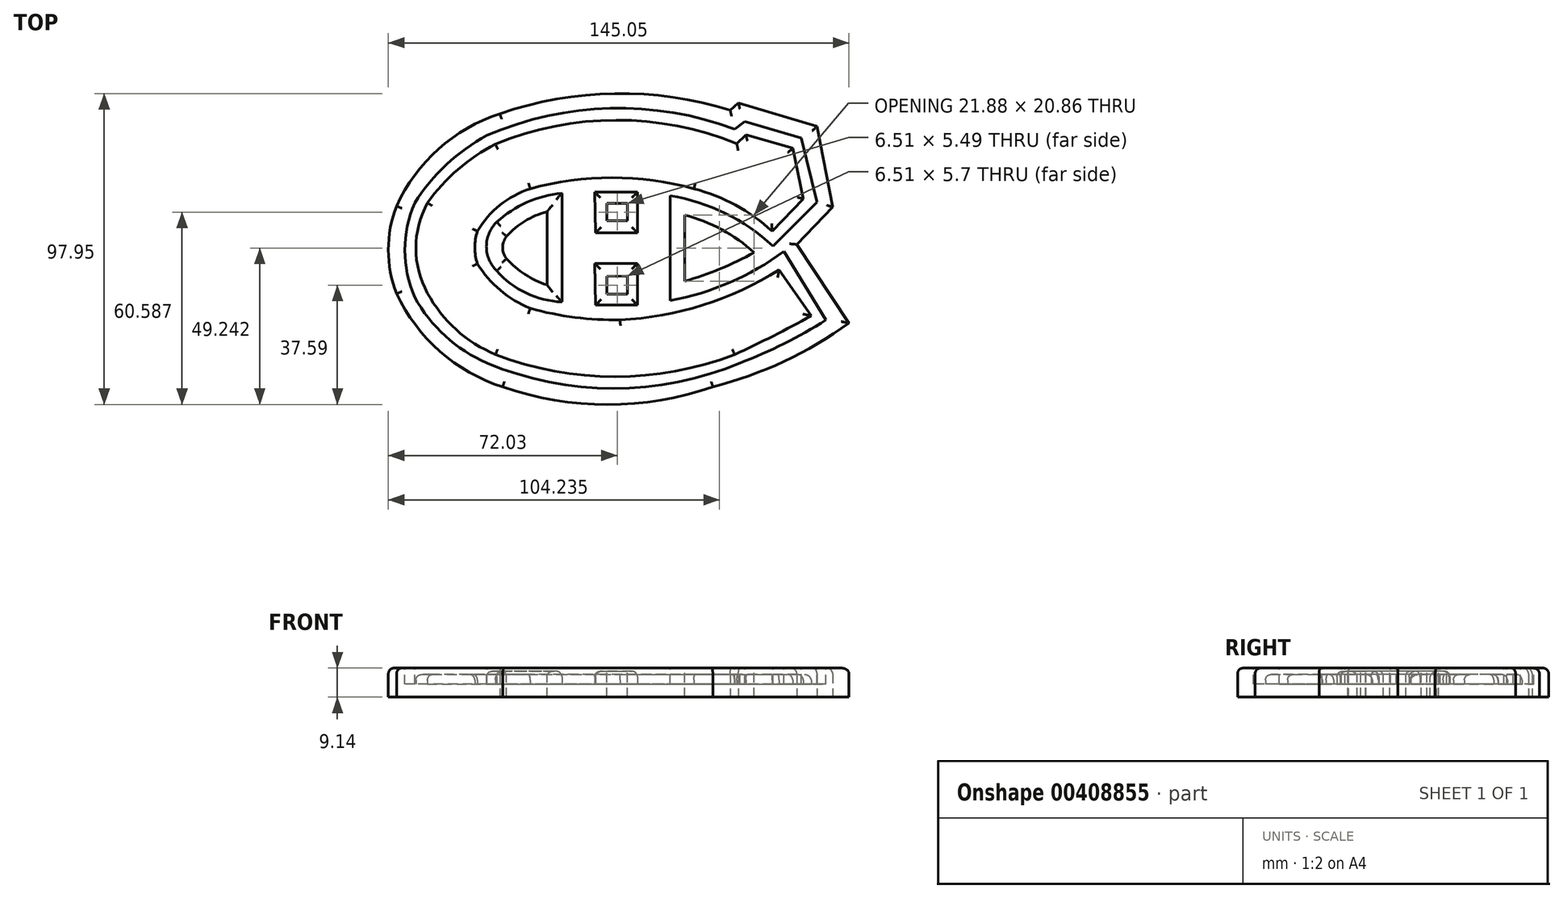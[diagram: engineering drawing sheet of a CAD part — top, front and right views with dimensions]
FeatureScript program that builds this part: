
annotation { "Feature Type Name" : "Feature", "Feature Type Description" : "" }
export const myFeature = defineFeature(function(context is Context, id is Id, definition is map)
    precondition{}
    {
        {
            var Q0;
            Q0=qCreatedBy(makeId("Top.planeOp"),FACE);
            var sketch = newSketch(context, id + "F0", { "sketchPlane" : qUnion([Q0])});
            skArc(sketch, "E0", {"start": v(34.63, 46.82) * mm, "mid": v(-1.72, 52.03) * mm, "end": v(-37.9, 45.67) * mm});
            skArc(sketch, "E1", {"start": v(-37.9, 45.67) * mm, "mid": v(-57.2, 34.55) * mm, "end": v(-70.42, 16.6) * mm});
            skArc(sketch, "E2", {"start": v(-70.42, 16.6) * mm, "mid": v(-73, 2.79) * mm, "end": v(-70.42, -11.03) * mm});
            skArc(sketch, "E3", {"start": v(-70.42, -11.03) * mm, "mid": v(-56.74, -29.14) * mm, "end": v(-37.03, -40.38) * mm});
            skArc(sketch, "E4", {"start": v(-37.03, -40.38) * mm, "mid": v(-3.93, -45.9) * mm, "end": v(29.16, -40.38) * mm});
            skArc(sketch, "E5", {"start": v(29.16, -40.38) * mm, "mid": v(51.55, -32.32) * mm, "end": v(72.05, -20.24) * mm});
            skLineSegment(sketch, "E6", {"start": v(55.64, 4.52) * mm, "end": v(72.05, -20.24) * mm});
            skLineSegment(sketch, "E7", {"start": v(55.64, 4.52) * mm, "end": v(66.87, 16.32) * mm});
            skLineSegment(sketch, "E8", {"start": v(66.87, 16.32) * mm, "end": v(61.97, 41.64) * mm});
            skLineSegment(sketch, "E9", {"start": v(61.97, 41.64) * mm, "end": v(37.22, 49.13) * mm});
            skLineSegment(sketch, "E10", {"start": v(37.22, 49.13) * mm, "end": v(34.63, 46.82) * mm});
            skSolve(sketch);
        }
        {
            var Q0;
            Q0=makeQuery(id+"F0.imprint","IMPRINT",FACE,{"disambiguationData":[TD([[makeQuery(id+"F0.imprint","IMPRINT",EDGE,{"derivedFrom":sQuery(id+"F0.wireOp",EDGE,"E0")}),1.0]])]});
            extrude(context, id + "F1", {"entities" : qUnion([Q0]), "depth" : 9.14 * mm});
        }
        {
            var Q0;
            Q0=makeQuery(id+"F1.opExtrude","CAP_FACE",FACE,{"disambiguationData":[OSD([sQuery(id+"F0.wireOp",EDGE,"E0"),sQuery(id+"F0.wireOp",EDGE,"E1"),sQuery(id+"F0.wireOp",EDGE,"E2"),sQuery(id+"F0.wireOp",EDGE,"E3"),sQuery(id+"F0.wireOp",EDGE,"E4"),sQuery(id+"F0.wireOp",EDGE,"E5"),sQuery(id+"F0.wireOp",EDGE,"E6"),sQuery(id+"F0.wireOp",EDGE,"E7"),sQuery(id+"F0.wireOp",EDGE,"E8"),sQuery(id+"F0.wireOp",EDGE,"E9"),sQuery(id+"F0.wireOp",EDGE,"E10")])],"isStart":false});
            var sketch = newSketch(context, id + "F2", { "sketchPlane" : qUnion([Q0])});
            skArc(sketch, "E11", {"start": v(36, 40.87) * mm, "mid": v(-3.18, 47.38) * mm, "end": v(-41.99, 38.85) * mm});
            skArc(sketch, "E12", {"start": v(-41.99, 38.85) * mm, "mid": v(-54.71, 29.65) * mm, "end": v(-64.72, 17.56) * mm});
            skArc(sketch, "E13", {"start": v(-64.72, 17.56) * mm, "mid": v(-67.78, 2.73) * mm, "end": v(-64.72, -12.09) * mm});
            skArc(sketch, "E14", {"start": v(-64.72, -12.09) * mm, "mid": v(-55.07, -24.33) * mm, "end": v(-41.99, -32.8) * mm});
            skArc(sketch, "E15", {"start": v(-41.99, -32.8) * mm, "mid": v(-2.12, -40.85) * mm, "end": v(37.74, -32.8) * mm});
            skArc(sketch, "E16", {"start": v(37.74, -32.8) * mm, "mid": v(51.6, -26.7) * mm, "end": v(64.8, -19.28) * mm});
            skLineSegment(sketch, "E17", {"start": v(48.1, 4.03) * mm, "end": v(61.91, 17.84) * mm});
            skLineSegment(sketch, "E18", {"start": v(61.91, 17.84) * mm, "end": v(57.02, 38) * mm});
            skLineSegment(sketch, "E19", {"start": v(57.02, 38) * mm, "end": v(39.18, 43.17) * mm});
            skLineSegment(sketch, "E20", {"start": v(39.18, 43.17) * mm, "end": v(36, 40.87) * mm});
            skLineSegment(sketch, "E21", {"start": v(64.8, -19.28) * mm, "end": v(51.55, 2.3) * mm});
            skArc(sketch, "E22", {"start": v(15.77, -13.17) * mm, "mid": v(34.54, -7.45) * mm, "end": v(51.55, 2.3) * mm});
            skLineSegment(sketch, "E23", {"start": v(15.77, -13.17) * mm, "end": v(15.77, 19.88) * mm});
            skArc(sketch, "E24", {"start": v(48.1, 4.03) * mm, "mid": v(33.1, 14.32) * mm, "end": v(15.77, 19.88) * mm});
            skSolve(sketch);
        }
        {
            var Q0;
            Q0 = qSketchRegion(id + "F2", true);
            extrude(context, id + "F3", {"entities" : qUnion([Q0]), "operationType" : NewBodyOperationType.REMOVE, "depth" : 7.62 * mm});
        }
        {
            var Q0;
            Q0 = qSketchRegion(id + "F2", true);
            extrude(context, id + "F4", {"entities" : qUnion([Q0]), "operationType" : NewBodyOperationType.REMOVE, "oppositeDirection" : true, "depth" : 5.08 * mm});
        }
        {
            var Q0;
            Q0=makeQuery(id+"F4.boolean.opBoolean","COPY",FACE,{"derivedFrom":makeQuery(id+"F4.opExtrude","CAP_FACE",FACE,{"disambiguationData":[OSD([sQuery(id+"F2.wireOp",EDGE,"E11"),sQuery(id+"F2.wireOp",EDGE,"E12"),sQuery(id+"F2.wireOp",EDGE,"E13"),sQuery(id+"F2.wireOp",EDGE,"E14"),sQuery(id+"F2.wireOp",EDGE,"E15"),sQuery(id+"F2.wireOp",EDGE,"E16"),sQuery(id+"F2.wireOp",EDGE,"E17"),sQuery(id+"F2.wireOp",EDGE,"E18"),sQuery(id+"F2.wireOp",EDGE,"E19"),sQuery(id+"F2.wireOp",EDGE,"E20"),sQuery(id+"F2.wireOp",EDGE,"E21"),sQuery(id+"F2.wireOp",EDGE,"E22"),sQuery(id+"F2.wireOp",EDGE,"E23"),sQuery(id+"F2.wireOp",EDGE,"E24")])],"isStart":false})});
            var sketch = newSketch(context, id + "F5", { "sketchPlane" : qUnion([Q0])});
            skLineSegment(sketch, "E25", {"start": v(-18.34, 20.64) * mm, "end": v(-18.34, -13.58) * mm});
            skLineSegment(sketch, "E26", {"start": v(-8.05, 20.99) * mm, "end": v(5.45, 20.99) * mm});
            skLineSegment(sketch, "E27", {"start": v(5.45, 20.99) * mm, "end": v(5.45, 8.15) * mm});
            skLineSegment(sketch, "E28", {"start": v(5.45, 8.15) * mm, "end": v(-7.73, 8.15) * mm});
            skLineSegment(sketch, "E29", {"start": v(-7.73, 8.15) * mm, "end": v(-8.05, 20.99) * mm});
            skLineSegment(sketch, "E30", {"start": v(-8.07, -1.43) * mm, "end": v(5.45, -1.43) * mm});
            skLineSegment(sketch, "E31", {"start": v(5.45, -1.43) * mm, "end": v(5.45, -14.6) * mm});
            skLineSegment(sketch, "E32", {"start": v(5.45, -14.6) * mm, "end": v(-7.73, -14.6) * mm});
            skLineSegment(sketch, "E33", {"start": v(-7.73, -14.6) * mm, "end": v(-8.07, -1.43) * mm});
            skArc(sketch, "E34", {"start": v(-18.34, 20.64) * mm, "mid": v(-29.35, 17.8) * mm, "end": v(-38.87, 11.57) * mm});
            skArc(sketch, "E35", {"start": v(-38.87, 11.57) * mm, "mid": v(-42.12, 3.87) * mm, "end": v(-38.87, -3.83) * mm});
            skArc(sketch, "E36", {"start": v(-38.87, -3.83) * mm, "mid": v(-29.6, -10.8) * mm, "end": v(-18.34, -13.58) * mm});
            skSolve(sketch);
        }
        {
            var Q0;
            Q0 = qSketchRegion(id + "F5", true);
            extrude(context, id + "F6", {"entities" : qUnion([Q0]), "operationType" : NewBodyOperationType.ADD, "depth" : 4.06 * mm});
        }
        {
            var Q0;
            {var subQ0=sQuery(id+"F2.wireOp",EDGE,"E24");var subQ1=sQuery(id+"F2.wireOp",EDGE,"E23");var subQ2=sQuery(id+"F2.wireOp",EDGE,"E22");var subQ3=sQuery(id+"F2.wireOp",EDGE,"E21");var subQ4=sQuery(id+"F2.wireOp",EDGE,"E14");var subQ5=sQuery(id+"F2.wireOp",EDGE,"E13");var subQ6=sQuery(id+"F2.wireOp",EDGE,"E12");var subQ7=sQuery(id+"F2.wireOp",EDGE,"E11");var subQ8=sQuery(id+"F2.wireOp",EDGE,"E15");var subQ9=sQuery(id+"F2.wireOp",EDGE,"E16");var subQ10=sQuery(id+"F2.wireOp",EDGE,"E17");var subQ11=sQuery(id+"F2.wireOp",EDGE,"E18");var subQ12=sQuery(id+"F2.wireOp",EDGE,"E19");var subQ13=sQuery(id+"F2.wireOp",EDGE,"E20");Q0=makeQuery(id+"F6.boolean.opBoolean","SPLIT",FACE,{"disambiguationData":[TD([makeQuery(id+"F4.boolean.opBoolean","COPY",FACE,{"derivedFrom":makeQuery(id+"F4.opExtrude","SWEPT_FACE",FACE,{"disambiguationData":[OSD([subQ7])]})})])],"derivedFrom":makeQuery(id+"F4.boolean.opBoolean","COPY",FACE,{"derivedFrom":makeQuery(id+"F4.opExtrude","CAP_FACE",FACE,{"disambiguationData":[OSD([subQ7,subQ6,subQ5,subQ4,subQ8,subQ9,subQ10,subQ11,subQ12,subQ13,subQ3,subQ2,subQ1,subQ0])],"isStart":false})})});}
            var sketch = newSketch(context, id + "F7", { "sketchPlane" : qUnion([Q0])});
            skArc(sketch, "E37", {"start": v(36.7, 36.24) * mm, "mid": v(-1.3, 43.67) * mm, "end": v(-39.27, 36.07) * mm});
            skArc(sketch, "E38", {"start": v(-39.27, 36.07) * mm, "mid": v(-51.09, 28.12) * mm, "end": v(-60.67, 17.59) * mm});
            skArc(sketch, "E39", {"start": v(-60.67, 17.59) * mm, "mid": v(-64.33, 3.38) * mm, "end": v(-60.67, -10.82) * mm});
            skArc(sketch, "E40", {"start": v(-60.67, -10.82) * mm, "mid": v(-51.63, -22.33) * mm, "end": v(-39.27, -30.16) * mm});
            skArc(sketch, "E41", {"start": v(-39.27, -30.16) * mm, "mid": v(-1.63, -37.13) * mm, "end": v(36, -30.16) * mm});
            skArc(sketch, "E42", {"start": v(36, -30.16) * mm, "mid": v(48.18, -24.29) * mm, "end": v(60.15, -18) * mm});
            skArc(sketch, "E43", {"start": v(0, -19.2) * mm, "mid": v(26.06, -14.62) * mm, "end": v(50.06, -3.46) * mm});
            skArc(sketch, "E44", {"start": v(-28.32, -15.61) * mm, "mid": v(-14.3, -18.45) * mm, "end": v(0, -19.2) * mm});
            skArc(sketch, "E45", {"start": v(-44.92, -1.58) * mm, "mid": v(-37.74, -9.92) * mm, "end": v(-28.32, -15.61) * mm});
            skArc(sketch, "E46", {"start": v(-44.92, 8.69) * mm, "mid": v(-45.77, 3.55) * mm, "end": v(-44.92, -1.58) * mm});
            skArc(sketch, "E47", {"start": v(-28.32, 22.04) * mm, "mid": v(-37.86, 16.9) * mm, "end": v(-44.92, 8.69) * mm});
            skArc(sketch, "E48", {"start": v(23.19, 22.04) * mm, "mid": v(-2.57, 25.54) * mm, "end": v(-28.32, 22.04) * mm});
            skArc(sketch, "E49", {"start": v(47.83, 8.69) * mm, "mid": v(36.34, 16.9) * mm, "end": v(23.19, 22.04) * mm});
            skLineSegment(sketch, "E50", {"start": v(36.7, 36.24) * mm, "end": v(39.55, 39.08) * mm});
            skLineSegment(sketch, "E51", {"start": v(39.55, 39.08) * mm, "end": v(54.3, 34.8) * mm});
            skLineSegment(sketch, "E52", {"start": v(54.3, 34.8) * mm, "end": v(57.66, 18.83) * mm});
            skLineSegment(sketch, "E53", {"start": v(57.66, 18.83) * mm, "end": v(47.83, 8.69) * mm});
            skLineSegment(sketch, "E54", {"start": v(50.06, -3.46) * mm, "end": v(60.15, -18) * mm});
            skSolve(sketch);
        }
        {
            var Q0;
            Q0 = qSketchRegion(id + "F7", true);
            extrude(context, id + "F8", {"entities" : qUnion([Q0]), "operationType" : NewBodyOperationType.ADD, "depth" : 3.05 * mm});
        }
        {
            var Q0;
            Q0=makeQuery(id+"F1.opExtrude","CAP_FACE",FACE,{"disambiguationData":[OSD([sQuery(id+"F0.wireOp",EDGE,"E0"),sQuery(id+"F0.wireOp",EDGE,"E1"),sQuery(id+"F0.wireOp",EDGE,"E2"),sQuery(id+"F0.wireOp",EDGE,"E3"),sQuery(id+"F0.wireOp",EDGE,"E4"),sQuery(id+"F0.wireOp",EDGE,"E5"),sQuery(id+"F0.wireOp",EDGE,"E6"),sQuery(id+"F0.wireOp",EDGE,"E7"),sQuery(id+"F0.wireOp",EDGE,"E8"),sQuery(id+"F0.wireOp",EDGE,"E9"),sQuery(id+"F0.wireOp",EDGE,"E10")])],"isStart":false});
            var sketch = newSketch(context, id + "F9", { "sketchPlane" : qUnion([Q0])});
            skLineSegment(sketch, "E55", {"start": v(-4.23, 17.43) * mm, "end": v(2.29, 17.43) * mm});
            skLineSegment(sketch, "E56", {"start": v(2.29, 17.43) * mm, "end": v(2.29, 11.94) * mm});
            skLineSegment(sketch, "E57", {"start": v(-4.23, 17.43) * mm, "end": v(-4.23, 11.94) * mm});
            skLineSegment(sketch, "E58", {"start": v(-4.23, 11.94) * mm, "end": v(2.29, 11.94) * mm});
            skLineSegment(sketch, "E59", {"start": v(-4.23, -5.56) * mm, "end": v(-4.23, -11.16) * mm});
            skLineSegment(sketch, "E60", {"start": v(-4.23, -11.16) * mm, "end": v(2.29, -11.16) * mm});
            skLineSegment(sketch, "E61", {"start": v(2.29, -11.16) * mm, "end": v(2.29, -5.46) * mm});
            skLineSegment(sketch, "E62", {"start": v(2.29, -5.46) * mm, "end": v(-4.23, -5.56) * mm});
            skLineSegment(sketch, "E63", {"start": v(-23.05, 14.79) * mm, "end": v(-23.05, -8.2) * mm});
            skLineSegment(sketch, "E64", {"start": v(20.3, 13.77) * mm, "end": v(20.3, -7.09) * mm});
            skArc(sketch, "E65", {"start": v(-23.05, 14.79) * mm, "mid": v(-29.99, 11.87) * mm, "end": v(-35.77, 7.06) * mm});
            skArc(sketch, "E66", {"start": v(-35.77, 7.06) * mm, "mid": v(-37, 3.53) * mm, "end": v(-35.77, 0) * mm});
            skArc(sketch, "E67", {"start": v(-35.77, 0) * mm, "mid": v(-29.97, -4.97) * mm, "end": v(-23.05, -8.2) * mm});
            skArc(sketch, "E68", {"start": v(42.17, 1.97) * mm, "mid": v(31.95, 9.2) * mm, "end": v(20.3, 13.77) * mm});
            skArc(sketch, "E69", {"start": v(20.3, -7.09) * mm, "mid": v(31.49, -3.17) * mm, "end": v(42.17, 1.97) * mm});
            skSolve(sketch);
        }
        {
            var Q0;
            Q0 = qSketchRegion(id + "F9", true);
            extrude(context, id + "F10", {"entities" : qUnion([Q0]), "operationType" : NewBodyOperationType.REMOVE, "oppositeDirection" : true, "depth" : 25.4 * mm});
        }
        {
            var Q0;
            Q0=makeQuery(id+"F1.opExtrude","CAP_EDGE",EDGE,{"disambiguationData":[OSD([sQuery(id+"F0.wireOp",EDGE,"E0")])],"isStart":false});
            var Q1;
            Q1=makeQuery(id+"F1.opExtrude","CAP_EDGE",EDGE,{"disambiguationData":[OSD([sQuery(id+"F0.wireOp",EDGE,"E1")])],"isStart":false});
            var Q2;
            Q2=makeQuery(id+"F1.opExtrude","CAP_EDGE",EDGE,{"disambiguationData":[OSD([sQuery(id+"F0.wireOp",EDGE,"E2")])],"isStart":false});
            var Q3;
            Q3=makeQuery(id+"F1.opExtrude","CAP_EDGE",EDGE,{"disambiguationData":[OSD([sQuery(id+"F0.wireOp",EDGE,"E3")])],"isStart":false});
            var Q4;
            Q4=makeQuery(id+"F1.opExtrude","CAP_EDGE",EDGE,{"disambiguationData":[OSD([sQuery(id+"F0.wireOp",EDGE,"E4")])],"isStart":false});
            var Q5;
            Q5=makeQuery(id+"F1.opExtrude","CAP_EDGE",EDGE,{"disambiguationData":[OSD([sQuery(id+"F0.wireOp",EDGE,"E5")])],"isStart":false});
            var Q6;
            Q6=makeQuery(id+"F1.opExtrude","CAP_EDGE",EDGE,{"disambiguationData":[OSD([sQuery(id+"F0.wireOp",EDGE,"E9")])],"isStart":false});
            var Q7;
            Q7=makeQuery(id+"F1.opExtrude","CAP_EDGE",EDGE,{"disambiguationData":[OSD([sQuery(id+"F0.wireOp",EDGE,"E10")])],"isStart":false});
            var Q8;
            Q8=makeQuery(id+"F1.opExtrude","CAP_EDGE",EDGE,{"disambiguationData":[OSD([sQuery(id+"F0.wireOp",EDGE,"E8")])],"isStart":false});
            var Q9;
            Q9=makeQuery(id+"F1.opExtrude","CAP_EDGE",EDGE,{"disambiguationData":[OSD([sQuery(id+"F0.wireOp",EDGE,"E7")])],"isStart":false});
            var Q10;
            Q10=makeQuery(id+"F1.opExtrude","CAP_EDGE",EDGE,{"disambiguationData":[OSD([sQuery(id+"F0.wireOp",EDGE,"E6")])],"isStart":false});
            var Q11;
            Q11=makeQuery(id+"F4.boolean.opBoolean","COPY",EDGE,{"derivedFrom":makeQuery(id+"F4.opExtrude","CAP_EDGE",EDGE,{"disambiguationData":[OSD([sQuery(id+"F2.wireOp",EDGE,"E11")])],"isStart":true})});
            var Q12;
            Q12=makeQuery(id+"F4.boolean.opBoolean","COPY",EDGE,{"derivedFrom":makeQuery(id+"F4.opExtrude","CAP_EDGE",EDGE,{"disambiguationData":[OSD([sQuery(id+"F2.wireOp",EDGE,"E20")])],"isStart":true})});
            var Q13;
            Q13=makeQuery(id+"F4.boolean.opBoolean","COPY",EDGE,{"derivedFrom":makeQuery(id+"F4.opExtrude","CAP_EDGE",EDGE,{"disambiguationData":[OSD([sQuery(id+"F2.wireOp",EDGE,"E19")])],"isStart":true})});
            var Q14;
            Q14=makeQuery(id+"F4.boolean.opBoolean","COPY",EDGE,{"derivedFrom":makeQuery(id+"F4.opExtrude","CAP_EDGE",EDGE,{"disambiguationData":[OSD([sQuery(id+"F2.wireOp",EDGE,"E18")])],"isStart":true})});
            var Q15;
            Q15=makeQuery(id+"F4.boolean.opBoolean","COPY",EDGE,{"derivedFrom":makeQuery(id+"F4.opExtrude","CAP_EDGE",EDGE,{"disambiguationData":[OSD([sQuery(id+"F2.wireOp",EDGE,"E17")])],"isStart":true})});
            var Q16;
            Q16=makeQuery(id+"F4.boolean.opBoolean","COPY",EDGE,{"derivedFrom":makeQuery(id+"F4.opExtrude","CAP_EDGE",EDGE,{"disambiguationData":[OSD([sQuery(id+"F2.wireOp",EDGE,"E21")])],"isStart":true})});
            var Q17;
            Q17=makeQuery(id+"F4.boolean.opBoolean","COPY",EDGE,{"derivedFrom":makeQuery(id+"F4.opExtrude","CAP_EDGE",EDGE,{"disambiguationData":[OSD([sQuery(id+"F2.wireOp",EDGE,"E22")])],"isStart":true})});
            var Q18;
            Q18=makeQuery(id+"F4.boolean.opBoolean","COPY",EDGE,{"derivedFrom":makeQuery(id+"F4.opExtrude","CAP_EDGE",EDGE,{"disambiguationData":[OSD([sQuery(id+"F2.wireOp",EDGE,"E24")])],"isStart":true})});
            var Q19;
            Q19=makeQuery(id+"F4.boolean.opBoolean","COPY",EDGE,{"derivedFrom":makeQuery(id+"F4.opExtrude","CAP_EDGE",EDGE,{"disambiguationData":[OSD([sQuery(id+"F2.wireOp",EDGE,"E23")])],"isStart":true})});
            var Q20;
            Q20=makeQuery(id+"F6.opExtrude","CAP_EDGE",EDGE,{"disambiguationData":[OSD([sQuery(id+"F5.wireOp",EDGE,"E25")])],"isStart":false});
            var Q21;
            Q21=makeQuery(id+"F6.opExtrude","CAP_EDGE",EDGE,{"disambiguationData":[OSD([sQuery(id+"F5.wireOp",EDGE,"E34")])],"isStart":false});
            var Q22;
            Q22=makeQuery(id+"F6.opExtrude","CAP_EDGE",EDGE,{"disambiguationData":[OSD([sQuery(id+"F5.wireOp",EDGE,"E35")])],"isStart":false});
            var Q23;
            Q23=makeQuery(id+"F6.opExtrude","CAP_EDGE",EDGE,{"disambiguationData":[OSD([sQuery(id+"F5.wireOp",EDGE,"E36")])],"isStart":false});
            var Q24;
            Q24=makeQuery(id+"F10.boolean.opBoolean","INTERSECT",EDGE,{"derivedFrom":[makeQuery(id+"F6.opExtrude","CAP_FACE",FACE,{"disambiguationData":[OSD([sQuery(id+"F5.wireOp",EDGE,"E25"),sQuery(id+"F5.wireOp",EDGE,"E34"),sQuery(id+"F5.wireOp",EDGE,"E35"),sQuery(id+"F5.wireOp",EDGE,"E36")])],"isStart":false}),makeQuery(id+"F10.opExtrude","SWEPT_FACE",FACE,{"disambiguationData":[OSD([sQuery(id+"F9.wireOp",EDGE,"E66")])]})]});
            var Q25;
            Q25=makeQuery(id+"F10.boolean.opBoolean","INTERSECT",EDGE,{"derivedFrom":[makeQuery(id+"F6.opExtrude","CAP_FACE",FACE,{"disambiguationData":[OSD([sQuery(id+"F5.wireOp",EDGE,"E25"),sQuery(id+"F5.wireOp",EDGE,"E34"),sQuery(id+"F5.wireOp",EDGE,"E35"),sQuery(id+"F5.wireOp",EDGE,"E36")])],"isStart":false}),makeQuery(id+"F10.opExtrude","SWEPT_FACE",FACE,{"disambiguationData":[OSD([sQuery(id+"F9.wireOp",EDGE,"E65")])]})]});
            var Q26;
            Q26=makeQuery(id+"F10.boolean.opBoolean","INTERSECT",EDGE,{"derivedFrom":[makeQuery(id+"F6.opExtrude","CAP_FACE",FACE,{"disambiguationData":[OSD([sQuery(id+"F5.wireOp",EDGE,"E25"),sQuery(id+"F5.wireOp",EDGE,"E34"),sQuery(id+"F5.wireOp",EDGE,"E35"),sQuery(id+"F5.wireOp",EDGE,"E36")])],"isStart":false}),makeQuery(id+"F10.opExtrude","SWEPT_FACE",FACE,{"disambiguationData":[OSD([sQuery(id+"F9.wireOp",EDGE,"E63")])]})]});
            var Q27;
            Q27=makeQuery(id+"F10.boolean.opBoolean","INTERSECT",EDGE,{"derivedFrom":[makeQuery(id+"F6.opExtrude","CAP_FACE",FACE,{"disambiguationData":[OSD([sQuery(id+"F5.wireOp",EDGE,"E25"),sQuery(id+"F5.wireOp",EDGE,"E34"),sQuery(id+"F5.wireOp",EDGE,"E35"),sQuery(id+"F5.wireOp",EDGE,"E36")])],"isStart":false}),makeQuery(id+"F10.opExtrude","SWEPT_FACE",FACE,{"disambiguationData":[OSD([sQuery(id+"F9.wireOp",EDGE,"E67")])]})]});
            var Q28;
            Q28=makeQuery(id+"F10.boolean.opBoolean","COPY",EDGE,{"derivedFrom":makeQuery(id+"F10.opExtrude","CAP_EDGE",EDGE,{"disambiguationData":[OSD([sQuery(id+"F9.wireOp",EDGE,"E68")])],"isStart":true})});
            var Q29;
            Q29=makeQuery(id+"F10.boolean.opBoolean","COPY",EDGE,{"derivedFrom":makeQuery(id+"F10.opExtrude","CAP_EDGE",EDGE,{"disambiguationData":[OSD([sQuery(id+"F9.wireOp",EDGE,"E64")])],"isStart":true})});
            var Q30;
            Q30=makeQuery(id+"F10.boolean.opBoolean","COPY",EDGE,{"derivedFrom":makeQuery(id+"F10.opExtrude","CAP_EDGE",EDGE,{"disambiguationData":[OSD([sQuery(id+"F9.wireOp",EDGE,"E69")])],"isStart":true})});
            var Q31;
            Q31=makeQuery(id+"F6.opExtrude","CAP_EDGE",EDGE,{"disambiguationData":[OSD([sQuery(id+"F5.wireOp",EDGE,"E31")])],"isStart":false});
            var Q32;
            Q32=makeQuery(id+"F6.opExtrude","CAP_EDGE",EDGE,{"disambiguationData":[OSD([sQuery(id+"F5.wireOp",EDGE,"E30")])],"isStart":false});
            var Q33;
            Q33=makeQuery(id+"F6.opExtrude","CAP_EDGE",EDGE,{"disambiguationData":[OSD([sQuery(id+"F5.wireOp",EDGE,"E33")])],"isStart":false});
            var Q34;
            Q34=makeQuery(id+"F6.opExtrude","CAP_EDGE",EDGE,{"disambiguationData":[OSD([sQuery(id+"F5.wireOp",EDGE,"E32")])],"isStart":false});
            var Q35;
            Q35=makeQuery(id+"F6.opExtrude","CAP_EDGE",EDGE,{"disambiguationData":[OSD([sQuery(id+"F5.wireOp",EDGE,"E28")])],"isStart":false});
            var Q36;
            Q36=makeQuery(id+"F6.opExtrude","CAP_EDGE",EDGE,{"disambiguationData":[OSD([sQuery(id+"F5.wireOp",EDGE,"E29")])],"isStart":false});
            var Q37;
            Q37=makeQuery(id+"F6.opExtrude","CAP_EDGE",EDGE,{"disambiguationData":[OSD([sQuery(id+"F5.wireOp",EDGE,"E26")])],"isStart":false});
            var Q38;
            Q38=makeQuery(id+"F6.opExtrude","CAP_EDGE",EDGE,{"disambiguationData":[OSD([sQuery(id+"F5.wireOp",EDGE,"E27")])],"isStart":false});
            var Q39;
            Q39=makeQuery(id+"F4.boolean.opBoolean","COPY",EDGE,{"derivedFrom":makeQuery(id+"F4.opExtrude","CAP_EDGE",EDGE,{"disambiguationData":[OSD([sQuery(id+"F2.wireOp",EDGE,"E12")])],"isStart":true})});
            var Q40;
            Q40=makeQuery(id+"F4.boolean.opBoolean","COPY",EDGE,{"derivedFrom":makeQuery(id+"F4.opExtrude","CAP_EDGE",EDGE,{"disambiguationData":[OSD([sQuery(id+"F2.wireOp",EDGE,"E13")])],"isStart":true})});
            var Q41;
            Q41=makeQuery(id+"F4.boolean.opBoolean","COPY",EDGE,{"derivedFrom":makeQuery(id+"F4.opExtrude","CAP_EDGE",EDGE,{"disambiguationData":[OSD([sQuery(id+"F2.wireOp",EDGE,"E14")])],"isStart":true})});
            var Q42;
            Q42=makeQuery(id+"F4.boolean.opBoolean","COPY",EDGE,{"derivedFrom":makeQuery(id+"F4.opExtrude","CAP_EDGE",EDGE,{"disambiguationData":[OSD([sQuery(id+"F2.wireOp",EDGE,"E15")])],"isStart":true})});
            var Q43;
            Q43=makeQuery(id+"F4.boolean.opBoolean","COPY",EDGE,{"derivedFrom":makeQuery(id+"F4.opExtrude","CAP_EDGE",EDGE,{"disambiguationData":[OSD([sQuery(id+"F2.wireOp",EDGE,"E16")])],"isStart":true})});
            var Q44;
            Q44=makeQuery(id+"F8.opExtrude","CAP_EDGE",EDGE,{"disambiguationData":[OSD([sQuery(id+"F7.wireOp",EDGE,"E37")])],"isStart":false});
            var Q45;
            Q45=makeQuery(id+"F8.opExtrude","CAP_EDGE",EDGE,{"disambiguationData":[OSD([sQuery(id+"F7.wireOp",EDGE,"E38")])],"isStart":false});
            var Q46;
            Q46=makeQuery(id+"F8.opExtrude","CAP_EDGE",EDGE,{"disambiguationData":[OSD([sQuery(id+"F7.wireOp",EDGE,"E50")])],"isStart":false});
            var Q47;
            Q47=makeQuery(id+"F8.opExtrude","CAP_EDGE",EDGE,{"disambiguationData":[OSD([sQuery(id+"F7.wireOp",EDGE,"E51")])],"isStart":false});
            var Q48;
            Q48=makeQuery(id+"F8.opExtrude","CAP_EDGE",EDGE,{"disambiguationData":[OSD([sQuery(id+"F7.wireOp",EDGE,"E52")])],"isStart":false});
            var Q49;
            Q49=makeQuery(id+"F8.opExtrude","CAP_EDGE",EDGE,{"disambiguationData":[OSD([sQuery(id+"F7.wireOp",EDGE,"E53")])],"isStart":false});
            var Q50;
            Q50=makeQuery(id+"F8.opExtrude","CAP_EDGE",EDGE,{"disambiguationData":[OSD([sQuery(id+"F7.wireOp",EDGE,"E49")])],"isStart":false});
            var Q51;
            Q51=makeQuery(id+"F8.opExtrude","CAP_EDGE",EDGE,{"disambiguationData":[OSD([sQuery(id+"F7.wireOp",EDGE,"E48")])],"isStart":false});
            var Q52;
            Q52=makeQuery(id+"F8.opExtrude","CAP_EDGE",EDGE,{"disambiguationData":[OSD([sQuery(id+"F7.wireOp",EDGE,"E47")])],"isStart":false});
            var Q53;
            Q53=makeQuery(id+"F8.opExtrude","CAP_EDGE",EDGE,{"disambiguationData":[OSD([sQuery(id+"F7.wireOp",EDGE,"E46")])],"isStart":false});
            var Q54;
            Q54=makeQuery(id+"F8.opExtrude","CAP_EDGE",EDGE,{"disambiguationData":[OSD([sQuery(id+"F7.wireOp",EDGE,"E45")])],"isStart":false});
            var Q55;
            Q55=makeQuery(id+"F8.opExtrude","CAP_EDGE",EDGE,{"disambiguationData":[OSD([sQuery(id+"F7.wireOp",EDGE,"E44")])],"isStart":false});
            var Q56;
            Q56=makeQuery(id+"F8.opExtrude","CAP_EDGE",EDGE,{"disambiguationData":[OSD([sQuery(id+"F7.wireOp",EDGE,"E54")])],"isStart":false});
            var Q57;
            Q57=makeQuery(id+"F8.opExtrude","CAP_EDGE",EDGE,{"disambiguationData":[OSD([sQuery(id+"F7.wireOp",EDGE,"E42")])],"isStart":false});
            var Q58;
            Q58=makeQuery(id+"F8.opExtrude","CAP_EDGE",EDGE,{"disambiguationData":[OSD([sQuery(id+"F7.wireOp",EDGE,"E41")])],"isStart":false});
            var Q59;
            Q59=makeQuery(id+"F8.opExtrude","CAP_EDGE",EDGE,{"disambiguationData":[OSD([sQuery(id+"F7.wireOp",EDGE,"E43")])],"isStart":false});
            var Q60;
            Q60=makeQuery(id+"F8.opExtrude","CAP_EDGE",EDGE,{"disambiguationData":[OSD([sQuery(id+"F7.wireOp",EDGE,"E40")])],"isStart":false});
            var Q61;
            Q61=makeQuery(id+"F8.opExtrude","CAP_EDGE",EDGE,{"disambiguationData":[OSD([sQuery(id+"F7.wireOp",EDGE,"E39")])],"isStart":false});
            fillet(context, id + "F11", {"entities" : qUnion([Q0, Q1, Q2, Q3, Q4, Q5, Q6, Q7, Q8, Q9, Q10, Q11, Q12, Q13, Q14, Q15, Q16, Q17, Q18, Q19, Q20, Q21, Q22, Q23, Q24, Q25, Q26, Q27, Q28, Q29, Q30, Q31, Q32, Q33, Q34, Q35, Q36, Q37, Q38, Q39, Q40, Q41, Q42, Q43, Q44, Q45, Q46, Q47, Q48, Q49, Q50, Q51, Q52, Q53, Q54, Q55, Q56, Q57, Q58, Q59, Q60, Q61]), "radius" : 1.78 * mm, "tangentPropagation" : true, "allowEdgeOverflow" : false});
        }
    });
